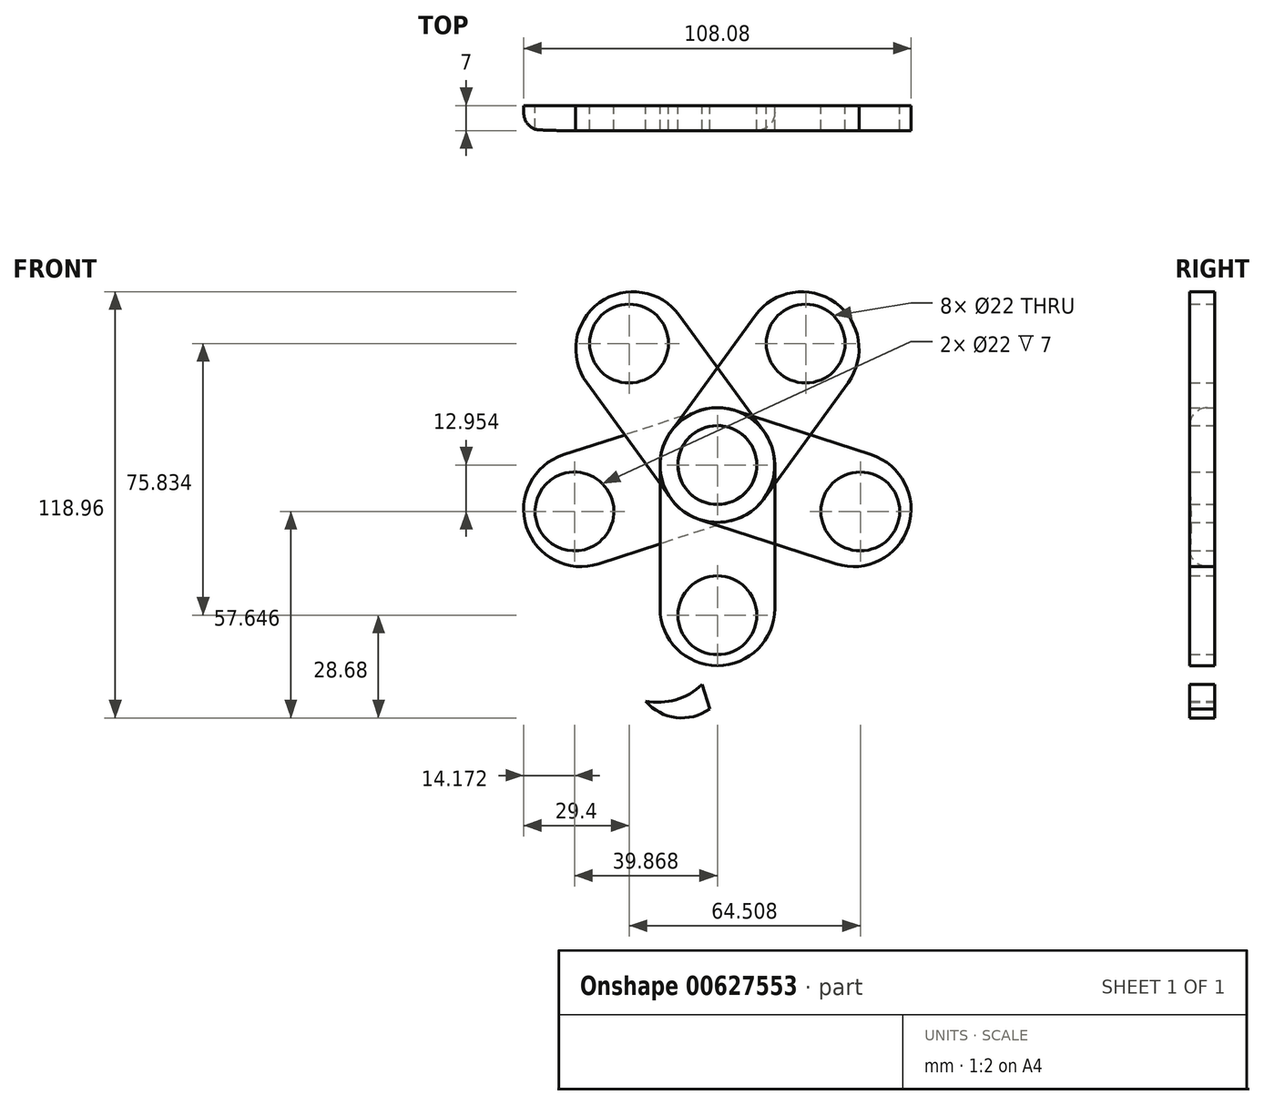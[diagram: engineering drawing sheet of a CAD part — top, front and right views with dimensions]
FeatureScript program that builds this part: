
annotation { "Feature Type Name" : "Feature", "Feature Type Description" : "" }
export const myFeature = defineFeature(function(context is Context, id is Id, definition is map)
    precondition{}
    {
        {
            var Q0;
            Q0=qCreatedBy(makeId("Front.planeOp"),FACE);
            var sketch = newSketch(context, id + "F0", { "sketchPlane" : qUnion([Q0])});
            skCircle(sketch, "E0", {"center": v(0, 0) * mm, "radius": 16 * mm});
            skCircle(sketch, "E1", {"center": v(0, -40) * mm, "radius": 16 * mm});
            skLineSegment(sketch, "E2", {"start": v(-16, 0) * mm, "end": v(-16, -40) * mm});
            skLineSegment(sketch, "E3", {"start": v(16, 0) * mm, "end": v(16, -40) * mm});
            skLineSegment(sketch, "E4", {"start": v(-6.42, -54.66) * mm, "end": v(0, -74.94) * mm});
            skLineSegment(sketch, "E5", {"start": v(0, -74.94) * mm, "end": v(8.3, -53.68) * mm});
            skArc(sketch, "E6", {"start": v(-20.01, -65.89) * mm, "mid": v(-11.52, -70.5) * mm, "end": v(-2.17, -68.08) * mm});
            skArc(sketch, "E7", {"start": v(-20.01, -65.89) * mm, "mid": v(-11.6, -65.52) * mm, "end": v(-4.31, -61.3) * mm});
            skArc(sketch, "E8", {"start": v(18.94, -69.73) * mm, "mid": v(14.03, -62.25) * mm, "end": v(5.1, -61.9) * mm});
            skArc(sketch, "E9", {"start": v(18.94, -69.73) * mm, "mid": v(11.63, -64.99) * mm, "end": v(3.13, -66.92) * mm});
            skSolve(sketch);
        }
        {
            var Q0;
            Q0=qSketchRegion(id+"F0",true);
            extrude(context, id + "F1", {"entities" : qUnion([Q0]), "depth" : 7 * mm, "offsetDistance" : 25 * mm});
        }
        {
            var Q0;
            Q0=qCreatedBy(makeId("Front.planeOp"),FACE);
            var sketch = newSketch(context, id + "F2", { "sketchPlane" : qUnion([Q0])});
            skCircle(sketch, "E10", {"center": v(0, 0) * mm, "radius": 11 * mm});
            skCircle(sketch, "E11", {"center": v(0, -41.92) * mm, "radius": 11 * mm});
            skSolve(sketch);
        }
        {
            var Q0;
            Q0=qSketchRegion(id+"F2",true);
            extrude(context, id + "F3", {"entities" : qUnion([Q0]), "operationType" : NewBodyOperationType.REMOVE, "endBound" : BoundingType.UP_TO_NEXT, "depth" : 25 * mm, "offsetDistance" : 25 * mm});
        }
        {
            var Q0;
            Q0=makeQuery(id+"F1.opExtrude","SWEPT_BODY",BODY,{"disambiguationData":[OSD([sQuery(id+"F0.wireOp",EDGE,"E0"),sQuery(id+"F0.wireOp",EDGE,"E1"),sQuery(id+"F0.wireOp",EDGE,"E2"),sQuery(id+"F0.wireOp",EDGE,"E3")])]});
            var Q1;
            Q1=makeQuery(id+"F1.opExtrude","SWEPT_FACE",FACE,{"disambiguationData":[OSD([sQuery(id+"F0.wireOp",EDGE,"E0")])]});
            circularPattern(context, id + "F4", {"entities" : qUnion([Q0]), "axis" : qUnion([Q1]), "angle" : 360 * degree, "instanceCount" : 5, "equalSpace" : true});
        }
        {
            var Q0;
            Q0=makeQuery(id+"F4.opPattern","COPY",EDGE,{"derivedFrom":makeQuery(id+"F1.opExtrude","CAP_EDGE",EDGE,{"disambiguationData":[OSD([sQuery(id+"F0.wireOp",EDGE,"E3")])],"isStart":false}),"instanceName":"1"});
            fillet(context, id + "F5", {"entities" : qUnion([Q0]), "radius" : 5 * mm, "tangentPropagation" : true, "allowEdgeOverflow" : false});
        }
    });
